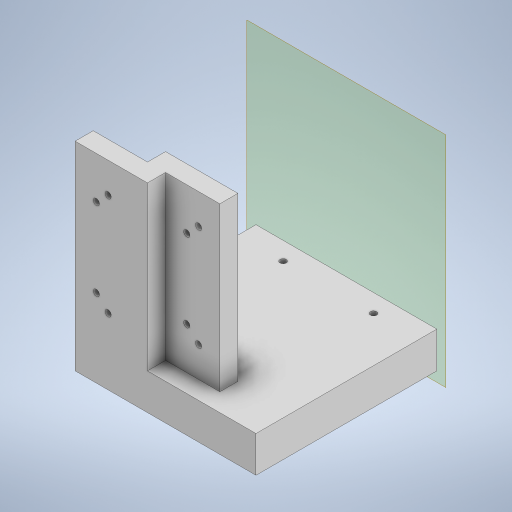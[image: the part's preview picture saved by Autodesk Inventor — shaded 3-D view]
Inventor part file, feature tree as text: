
AUTODESK INVENTOR PART (.ipt)
format: ipt  version: 2023 (Build 270158000, 158)  size: 343,552 bytes
history: native  units: mm
features: sketch x7, extrude x4, hole x3, other x1, mirror x1, plane x1, split x1
ambient origin geometry x8: Origin, YZ Plane, XZ Plane, XY Plane, X Axis, Y Axis, Z Axis, Center Point
bodies: Body1 (feature_tree)
feature tree (18):
  other  "Sólido1"
  extrude  "Extrusión1"  Depth=90.0mm
  hole  "Agujero1"  [1 undecoded]
  extrude  "Extrusión2"  TaperAngle=0.0deg  [1 undecoded]
  extrude  "Extrusión3"  Depth=90.0mm
  hole  "Agujero2"  [1 undecoded]
  extrude  "Extrusión4"  Depth=10.0mm TaperAngle=0.0deg
  mirror  "Simetría1"
  plane  "Plano de trabajo2"
  hole  "Agujero3"  [1 undecoded]
  split  "Dividir1"
  sketch  "Boceto1"  dims[d0=30.0mm d1=90.0mm]
  sketch  "Boceto2"  dims[d2=10.0mm d3=0.0mm]
  sketch  "Boceto3"  dims[d4=1.75mm d5=1.75mm d6=1.75mm d7=1.75mm d8=10.0mm d9=10.0mm d10=10.0mm d11=15.0mm d12=0.0mm]
  sketch  "Boceto4"  dims[d13=30.0mm d14=0.0mm]
  sketch  "Boceto5"  dims[d15=90.0mm d16=15.0mm]
  sketch  "Boceto6"  dims[d17=3.5mm d18=6.0mm d19=4.0mm d20=2.0mm d21=90.0deg d22=8.0mm d23=20.594885mm d24=20.0mm]
  sketch  "Boceto7"  dims[d25=90.0mm d26=10.0mm d27=0.0mm d28=30.0mm d29=0.0mm d30=3.5mm d31=1.75mm d32=1.75mm d33=1.75mm d34=1.75mm d35=10.0mm d36=10.0mm d38=10.0mm d39=-41.10961mm d40=15.0mm d41=0.0mm d42=15.0mm d43=90.0mm d45=0.0mm d46=3.5mm d47=6.0mm d48=4.0mm d49=2.0mm d50=90.0deg d51=8.0mm d52=20.594885mm d53=20.0mm d54=100.0mm d55=0.0mm d56=5.0mm d57=5.0mm d58=3.5mm d59=5.0mm d60=5.0mm d61=10.0mm d62=30.0mm d64=20.0mm d65=3.5mm d66=6.0mm d67=4.0mm d68=2.0mm d69=90.0deg d70=8.0mm d71=20.594885mm]
note: 4 required parameter values undecoded (feature->parameter linkage not recoverable at this tier; creation-order binding heuristic only, values carry confidence <= 0.55)
